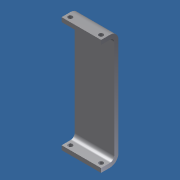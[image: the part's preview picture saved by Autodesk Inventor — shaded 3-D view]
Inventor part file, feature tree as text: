
AUTODESK INVENTOR PART (.ipt)
format: ipt  version: 2012 (Build 160160000, 160)  size: 118,784 bytes
history: native  units: in
note: dims shown in document units (in); Inventor stores cm internally (conversion verified against a paired STEP export)
features: sheet_metal_op x4, sketch x4, hole x2, other x2
ambient origin geometry x8: Origin, YZ Plane, XZ Plane, XY Plane, X Axis, Y Axis, Z Axis, Center Point
feature tree (12):
  sheet_metal_op  "Face2"
  sheet_metal_op  "Flange1"
  hole  "Hole1"  [1 undecoded]
  hole  "Hole2"  [1 undecoded]
  sketch  "Sketch1"  dims[d0=1.125in d1=3.28in]
  other  "Plate2"
  sketch  "Sketch2"  dims[d2=0.5625in d3=1.64in]
  other  "Plate3"
  sheet_metal_op  "Bend1"
  sheet_metal_op  "Corner1"
  sketch  "Sketch3"  dims[d4=0.12in]
  sketch  "Sketch5"  dims[d5=0.12in d6=0.12in d7=0.06in d8=0.24in d9=0.12in d10=0.375in d11=90.0deg d12=0.12in d13=0.48in d14=0.12in d15=0.12in d16=0.125in d17=0.125in d18=0.125in d19=0.125in d20=0.125in d21=0.75in d22=0.375in d23=0.25in d24=0.5635in d25=0.12in d26=0.8108in d27=0.125in d28=0.75in d29=0.375in d30=0.25in d31=0.5635in d32=0.12in d33=0.8108in]
note: 2 required parameter values undecoded (feature->parameter linkage not recoverable at this tier; creation-order binding heuristic only, values carry confidence <= 0.55)
